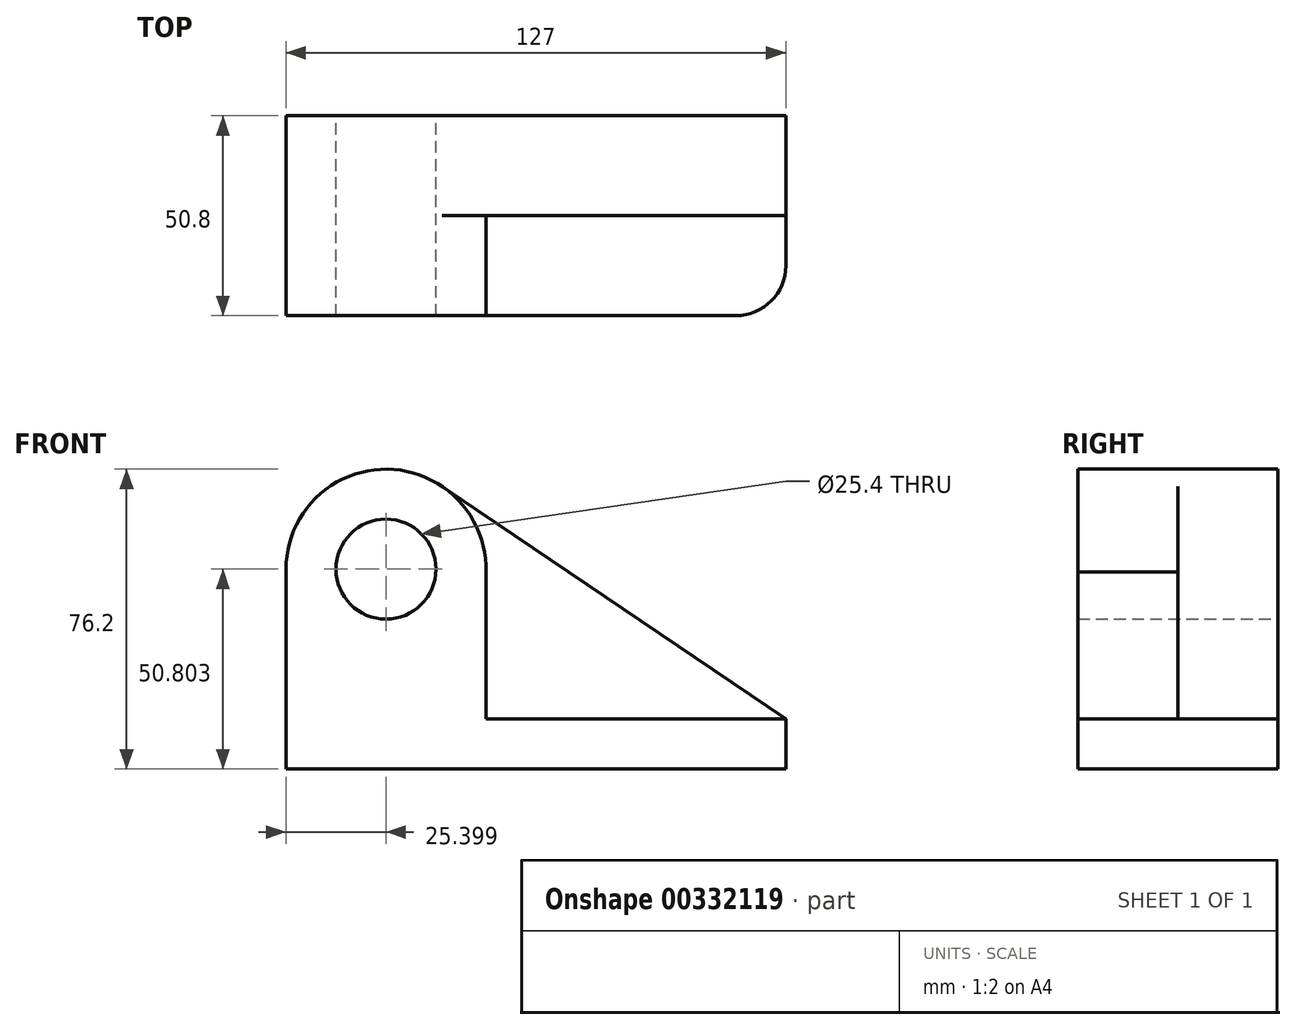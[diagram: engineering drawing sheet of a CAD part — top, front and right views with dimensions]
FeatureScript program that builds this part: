
annotation { "Feature Type Name" : "Feature", "Feature Type Description" : "" }
export const myFeature = defineFeature(function(context is Context, id is Id, definition is map)
    precondition{}
    {
        {
            var Q0;
            Q0=qCreatedBy(makeId("Front.planeOp"),FACE);
            var sketch = newSketch(context, id + "F0", { "sketchPlane" : qUnion([Q0])});
            skCircle(sketch, "E0", {"center": v(-39.64, 30.43) * mm, "radius": 12.7 * mm});
            skArc(sketch, "E1", {"start": v(-25.4, 51.47) * mm, "mid": v(-51.55, 52.87) * mm, "end": v(-65.04, 30.43) * mm});
            skLineSegment(sketch, "E2", {"start": v(-65.04, 30.43) * mm, "end": v(-65.04, -20.37) * mm});
            skLineSegment(sketch, "E3", {"start": v(-65.04, -20.37) * mm, "end": v(61.96, -20.37) * mm});
            skLineSegment(sketch, "E4", {"start": v(61.96, -20.37) * mm, "end": v(61.96, -7.67) * mm});
            skLineSegment(sketch, "E5", {"start": v(61.96, -7.67) * mm, "end": v(-25.4, 51.47) * mm});
            skSolve(sketch);
        }
        {
            var Q0;
            Q0=makeQuery(id+"F0.imprint","IMPRINT",FACE,{"disambiguationData":[TD([[makeQuery(id+"F0.imprint","IMPRINT",EDGE,{"derivedFrom":sQuery(id+"F0.wireOp",EDGE,"E0")}),-1.0]])]});
            extrude(context, id + "F1", {"entities" : qUnion([Q0]), "depth" : 25.4 * mm});
        }
        {
            var Q0;
            Q0=makeQuery(id+"F1.opExtrude","CAP_FACE",FACE,{"disambiguationData":[OSD([sQuery(id+"F0.wireOp",EDGE,"E0"),sQuery(id+"F0.wireOp",EDGE,"E1"),sQuery(id+"F0.wireOp",EDGE,"E2"),sQuery(id+"F0.wireOp",EDGE,"E3"),sQuery(id+"F0.wireOp",EDGE,"E4"),sQuery(id+"F0.wireOp",EDGE,"E5")])],"isStart":false});
            var sketch = newSketch(context, id + "F2", { "sketchPlane" : qUnion([Q0])});
            skCircle(sketch, "E6", {"center": v(-39.64, 30.43) * mm, "radius": 12.7 * mm});
            skLineSegment(sketch, "E7.bottom", {"start": v(61.96, -7.67) * mm, "end": v(-14.25, -7.67) * mm});
            skLineSegment(sketch, "E7.top", {"start": v(61.96, -20.37) * mm, "end": v(-65.04, -20.37) * mm});
            skLineSegment(sketch, "E7.left", {"start": v(61.96, -7.67) * mm, "end": v(61.96, -20.37) * mm});
            skLineSegment(sketch, "E7.right", {"start": v(-65.04, -7.67) * mm, "end": v(-65.04, -20.37) * mm});
            skLineSegment(sketch, "E8", {"start": v(-14.25, 29.71) * mm, "end": v(-14.25, -7.67) * mm});
            skCircle(sketch, "E9", {"center": v(-39.64, 30.43) * mm, "radius": 25.4 * mm});
            skSolve(sketch);
        }
        {
            var Q0;
            Q0=makeQuery(id+"F2.imprint","IMPRINT",FACE,{"disambiguationData":[TD([[makeQuery(id+"F2.imprint","IMPRINT",EDGE,{"derivedFrom":sQuery(id+"F2.wireOp",EDGE,"E6")}),-1.0]])]});
            extrude(context, id + "F3", {"entities" : qUnion([Q0]), "operationType" : NewBodyOperationType.ADD, "depth" : 25.4 * mm});
        }
        {
            var Q0;
            Q0=makeQuery(id+"F2.imprint","IMPRINT",FACE,{"disambiguationData":[TD([[makeQuery(id+"F2.imprint","IMPRINT",EDGE,{"derivedFrom":sQuery(id+"F2.wireOp",EDGE,"E6")}),-1.0]])]});
            extrude(context, id + "F4", {"entities" : qUnion([Q0]), "operationType" : NewBodyOperationType.ADD, "depth" : 25.4 * mm});
        }
        {
            var Q0;
            Q0=makeQuery(id+"F2.imprint","IMPRINT",FACE,{"disambiguationData":[TD([[makeQuery(id+"F2.imprint","IMPRINT",EDGE,{"derivedFrom":sQuery(id+"F2.wireOp",EDGE,"E7.bottom")}),1.0]])]});
            var Q1;
            Q1=makeQuery(id+"F2.imprint","IMPRINT",FACE,{"disambiguationData":[TD([[makeQuery(id+"F2.imprint","IMPRINT",EDGE,{"derivedFrom":sQuery(id+"F2.wireOp",EDGE,"E6")}),-1.0]])]});
            extrude(context, id + "F5", {"entities" : qUnion([Q0, Q1]), "operationType" : NewBodyOperationType.ADD, "depth" : 25.4 * mm});
        }
        {
            var Q0;
            Q0=makeQuery(id+"F5.opExtrude","CAP_EDGE",EDGE,{"disambiguationData":[OSD([sQuery(id+"F2.wireOp",EDGE,"E7.left")])],"isStart":false});
            fillet(context, id + "F6", {"entities" : qUnion([Q0]), "radius" : 12.7 * mm, "tangentPropagation" : true, "allowEdgeOverflow" : false});
        }
    });
